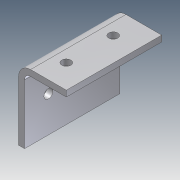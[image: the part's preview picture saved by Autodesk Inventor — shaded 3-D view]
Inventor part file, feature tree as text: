
AUTODESK INVENTOR PART (.ipt)
format: ipt  version: 2012 (Build 160160000, 160)  size: 97,792 bytes
history: native  units: in
note: dims shown in document units (in); Inventor stores cm internally (conversion verified against a paired STEP export)
features: hole x2, pattern_linear x2, extrude x1, sketch x1
ambient origin geometry x8: Origin, YZ Plane, XZ Plane, XY Plane, X Axis, Y Axis, Z Axis, Center Point
bodies: Solid1 (feature_tree)
feature tree (6):
  extrude  "Extrusion1"  Depth=1.5in
  hole  "Hole1"  [1 undecoded]
  pattern_linear  "Rectangular Pattern1"  Spacing1=0.25in  [1 undecoded]
  hole  "Hole2"  [1 undecoded]
  pattern_linear  "Rectangular Pattern2"  Spacing1=1.0in  [1 undecoded]
  sketch  "Sketch1"  dims[d0=0.125in d1=1.5in d2=0.125in d3=0.25in d4=2.0in d5=0.0in d6=1.0in d7=0.5in d8=0.5in d9=0.19in d10=0.75in d11=0.375in d12=0.25in d13=0.5635in d14=1.0in d15=0.8108in d16=0.7874in d18=0.9843in d19=0.5in d20=0.75in d21=0.19in d22=0.75in d23=0.375in d24=0.25in d25=0.5635in d26=1.0in d27=0.8108in d28=0.7874in d30=1.0in]
note: 4 required parameter values undecoded (feature->parameter linkage not recoverable at this tier; creation-order binding heuristic only, values carry confidence <= 0.55)
